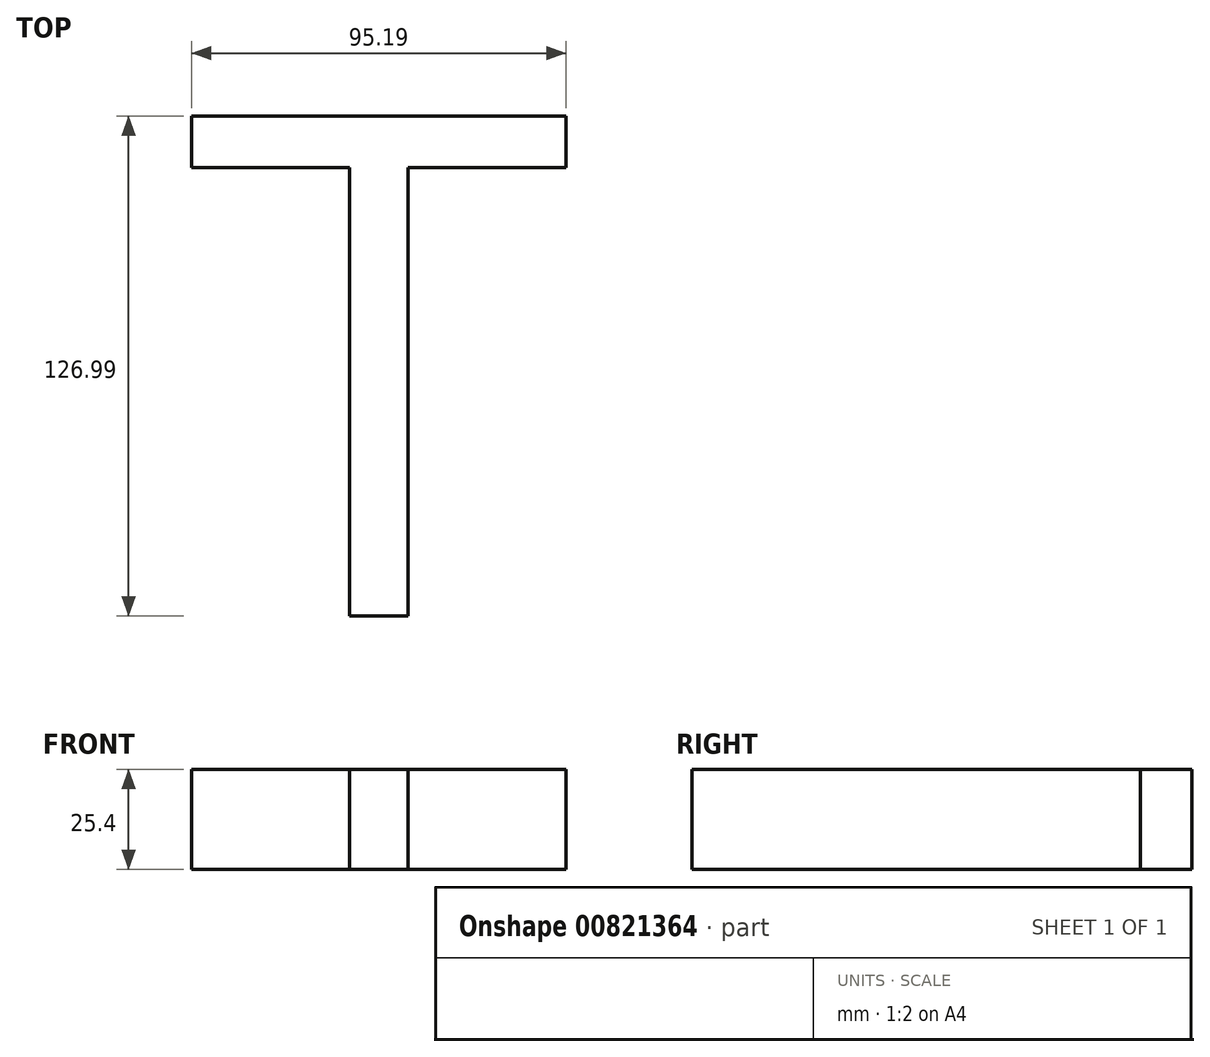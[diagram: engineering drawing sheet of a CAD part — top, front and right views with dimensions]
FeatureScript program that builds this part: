
annotation { "Feature Type Name" : "Feature", "Feature Type Description" : "" }
export const myFeature = defineFeature(function(context is Context, id is Id, definition is map)
    precondition{}
    {
        {
            var Q0;
            Q0=qCreatedBy(makeId("Top.planeOp"),FACE);
            var sketch = newSketch(context, id + "F0", { "sketchPlane" : qUnion([Q0])});
            skText(sketch, "E0", { "text": "T", "fontName": "OpenSans-Regular.ttf"});
            const initialGuessF0  = {"E0": [-0.0596, -0.06047, 1, 0, 0.12807]};
            skSetInitialGuess(sketch, initialGuessF0);
            skSolve(sketch);
        }
        {
            var Q0;
            Q0=makeQuery(id+"F0.imprint","IMPRINT",FACE,{"disambiguationData":[TD([[makeQuery(id+"F0.imprint","IMPRINT",EDGE,{"derivedFrom":sQuery(id+"F0.wireOp",EDGE,"E0.sketch_text.stroke-0")}),-1.0]])]});
            extrude(context, id + "F1", {"entities" : qUnion([Q0]), "depth" : 25.4 * mm, "offsetDistance" : 25.4 * mm});
        }
    });
